# Revit family: mucz-g2556_23_50hz
name_source: partatom
category: 機械設備
units: mm (PartAtom-declared; Revit-internal decimal feet)

## family parameters
OmniClass タイトル = Split System Air Conditioning Units
OmniClass 番号 = 23.75.10.24.21.27.27
パーツ タイプ = 標準
ロード時にボイドで切り取り = いいえ
丸型コネクタ寸法 = 直径を使用
作業面ベース = いいえ
共有 = いいえ
常に垂直 = はい
部屋計算ポイント = いいえ

## types (6) — shared parameters
Clearance Back = 100  [stored 0.328084 ft]
Clearance Left = 100  [stored 0.328084 ft]
Clearance Right = 350  [stored 1.14829 ft]
Clearance Top = 100  [stored 0.328084 ft]
FamilyVersion = v1.7
IfcExportAs = IfcUnitaryEquipmentType
IfcExportType = AIRCONDITIONINGUNIT
OmniClassCode = 23-33 17 13 11
URL = https://www.mitsubishielectric.co.jp
Uniclass2015Code = Pr_70_65_03_84
Uniclass2015Title = Split coil remote air cooled condensing units
Uniclass2015Version = Systems v1.9
ケーブル種類1 = VVF
サービススペース = はい
仕様書バージョン = Version1.0
企業コード = 108420
冷媒ガス管径 = 9.52 mm
冷媒液管径 = 6.35 mm
冷媒管径 = 100.00 mm
冷媒管径符号 = Ab
分類コード = 50053004206100
参照している仕様書等のバージョン = 公共建築物標準仕様書（機械設備工事編）平成31年度版
周波数 = 50 Hz
呼称 = パッケージ形空気調和機_室外機
始動方式 = 直入
形式 = パッケージ形 屋外機
推奨ブレーカー容量 = 15 A
最大電流値 = 0 A
本体マテリアル = <カテゴリ別>
極数 = 1
法定耐用年数 = 6
発停方法 = 付属スイッチ
相 = 1
積算_科目 = 1 空気調和設備
符号 = ACR
製品リリース年月 = -
製品出荷対象 = 国内
製造元 = 三菱電機株式会社
設置方法 = 床置形
説明 = ルームエアコン(霧ヶ峰) GVシリーズ 室外ユニット
負荷分類 = 10_ファンコイル類
運転方法 = 冷暖切替
運転質量 = 0.00 kg
zero-valued in all types: Clearance Bottom, ドレン　位置X, 価格

## per-type parameters (varying)
- 室外機_MUCZ-G2223(E,EE): APF=5.8; COP=4.02; Clearance Front=100  [stored 0.328084 ft]; Depth=249  [stored 0.816929 ft]; Height=453  [stored 1.48622 ft]; MAX風量=1370.0 m³/h; Width=679  [stored 2.22769 ft]; ドレン　位置Y=44  [stored 0.144357 ft]; ドレン　位置Z=23.5  [stored 0.0770997 ft]; ドレン管径=42.00 mm; モデル=MUCZ-G22**; 冷媒　位置X=361.5  [stored 1.18602 ft]; 冷媒　位置Y=136; 冷媒　位置Z=128.5  [stored 0.421588 ft]; 冷房 風量=1370.0 m³/h; 冷房能力=2 kW; 形名=MUCZ-G2223; 暖房 風量=1265.0 m³/h; 暖房能力=2 kW; 製品質量=19.00 kg; 質量=22.80 kg; 運転音(強冷房)  db=59; 運転音(強暖房)  db=59; 電動機出力_圧縮機=600 W; 電動機出力_送風機=22 W; 電圧=100 V; 音響パワーレベル(dB)=59; 風量=1370.0 m³/h
- 室外機_MUCZ-G2523(E,EE): APF=5.8; COP=3.92; Clearance Front=100  [stored 0.328084 ft]; Depth=249  [stored 0.816929 ft]; Height=453  [stored 1.48622 ft]; MAX風量=1690.0 m³/h; Width=679  [stored 2.22769 ft]; ドレン　位置Y=44  [stored 0.144357 ft]; ドレン　位置Z=23.5  [stored 0.0770997 ft]; ドレン管径=42.00 mm; モデル=MUCZ-G25**; 冷媒　位置X=361.5  [stored 1.18602 ft]; 冷媒　位置Y=136; 冷媒　位置Z=128.5  [stored 0.421588 ft]; 冷房 風量=1690.0 m³/h; 冷房能力=3 kW; 形名=MUCZ-G2523_2823; 暖房 風量=1490.0 m³/h; 暖房能力=3 kW; 製品質量=19.00 kg; 質量=22.80 kg; 運転音(強冷房)  db=61; 運転音(強暖房)  db=60; 電動機出力_圧縮機=650 W; 電動機出力_送風機=22 W; 電圧=100 V; 音響パワーレベル(dB)=61; 風量=1690.0 m³/h
- 室外機_MUCZ-G2823(E,EE): APF=5.8; COP=3.73; Clearance Front=100  [stored 0.328084 ft]; Depth=249  [stored 0.816929 ft]; Height=453  [stored 1.48622 ft]; MAX風量=1710.0 m³/h; Width=679  [stored 2.22769 ft]; ドレン　位置Y=44  [stored 0.144357 ft]; ドレン　位置Z=23.5  [stored 0.0770997 ft]; ドレン管径=42.00 mm; モデル=MUCZ-G28**; 冷媒　位置X=361.5  [stored 1.18602 ft]; 冷媒　位置Y=136; 冷媒　位置Z=128.5  [stored 0.421588 ft]; 冷房 風量=1710.0 m³/h; 冷房能力=3 kW; 形名=MUCZ-G2523_2823; 暖房 風量=1600.0 m³/h; 暖房能力=4 kW; 製品質量=20.00 kg; 質量=24.00 kg; 運転音(強冷房)  db=62; 運転音(強暖房)  db=65; 電動機出力_圧縮機=750 W; 電動機出力_送風機=22 W; 電圧=100 V; 音響パワーレベル(dB)=65; 風量=1710.0 m³/h
- 室外機_MUCZ-G3623(E,EE): APF=4.9; COP=3; Clearance Front=100  [stored 0.328084 ft]; Depth=249  [stored 0.816929 ft]; Height=538  [stored 1.76509 ft]; MAX風量=2110.0 m³/h; Width=699  [stored 2.29331 ft]; ドレン　位置Y=42  [stored 0.137795 ft]; ドレン　位置Z=23.5  [stored 0.0770997 ft]; ドレン管径=33.00 mm; モデル=MUCZ-G36**; 冷媒　位置X=371.5  [stored 1.21883 ft]; 冷媒　位置Y=121  [stored 0.396982 ft]; 冷媒　位置Z=130.5; 冷房 風量=2110.0 m³/h; 冷房能力=4 kW; 形名=MUCZ-G3623; 暖房 風量=2015.0 m³/h; 暖房能力=4 kW; 製品質量=23.00 kg; 質量=27.60 kg; 運転音(強冷房)  db=61; 運転音(強暖房)  db=64; 電動機出力_圧縮機=950 W; 電動機出力_送風機=22 W; 電圧=100 V; 音響パワーレベル(dB)=64; 風量=2110.0 m³/h
- 室外機_MUCZ-G4023S(E,EE): APF=4.9; COP=2.9; Clearance Front=200  [stored 0.656168 ft]; Depth=285  [stored 0.935039 ft]; Height=550  [stored 1.80446 ft]; MAX風量=2280.0 m³/h; Width=800  [stored 2.62467 ft]; ドレン　位置Y=44  [stored 0.144357 ft]; ドレン　位置Z=45  [stored 0.147638 ft]; ドレン管径=42.00 mm; モデル=MUCZ-G40**S; 冷媒　位置X=429  [stored 1.40748 ft]; 冷媒　位置Y=171  [stored 0.561024 ft]; 冷媒　位置Z=132.5  [stored 0.434711 ft]; 冷房 風量=2280.0 m³/h; 冷房能力=4 kW; 形名=MUCZ-G4023S_5623S; 暖房 風量=2280.0 m³/h; 暖房能力=5 kW; 製品質量=28.00 kg; 質量=33.60 kg; 運転音(強冷房)  db=61; 運転音(強暖房)  db=64; 電動機出力_圧縮機=1100 W; 電動機出力_送風機=50 W; 電圧=200 V; 音響パワーレベル(dB)=64; 風量=2280.0 m³/h
- 室外機_MUCZ-G5623S(E,EE): APF=5; COP=2.87; Clearance Front=200  [stored 0.656168 ft]; Depth=285  [stored 0.935039 ft]; Height=550  [stored 1.80446 ft]; MAX風量=2040.0 m³/h; Width=800  [stored 2.62467 ft]; ドレン　位置Y=44  [stored 0.144357 ft]; ドレン　位置Z=45  [stored 0.147638 ft]; ドレン管径=42.00 mm; モデル=MUCZ-G56**S; 冷媒　位置X=429  [stored 1.40748 ft]; 冷媒　位置Y=171  [stored 0.561024 ft]; 冷媒　位置Z=132.5  [stored 0.434711 ft]; 冷房 風量=2040.0 m³/h; 冷房能力=6 kW; 形名=MUCZ-G4023S_5623S; 暖房 風量=2135.0 m³/h; 暖房能力=7 kW; 製品質量=34.00 kg; 質量=40.80 kg; 運転音(強冷房)  db=65; 運転音(強暖房)  db=68; 電動機出力_圧縮機=1500 W; 電動機出力_送風機=50 W; 電圧=200 V; 音響パワーレベル(dB)=68; 風量=2040.0 m³/h

note: [stored X ft] marks values corroborated as IEEE doubles in the binary element streams (Revit-internal decimal feet)
